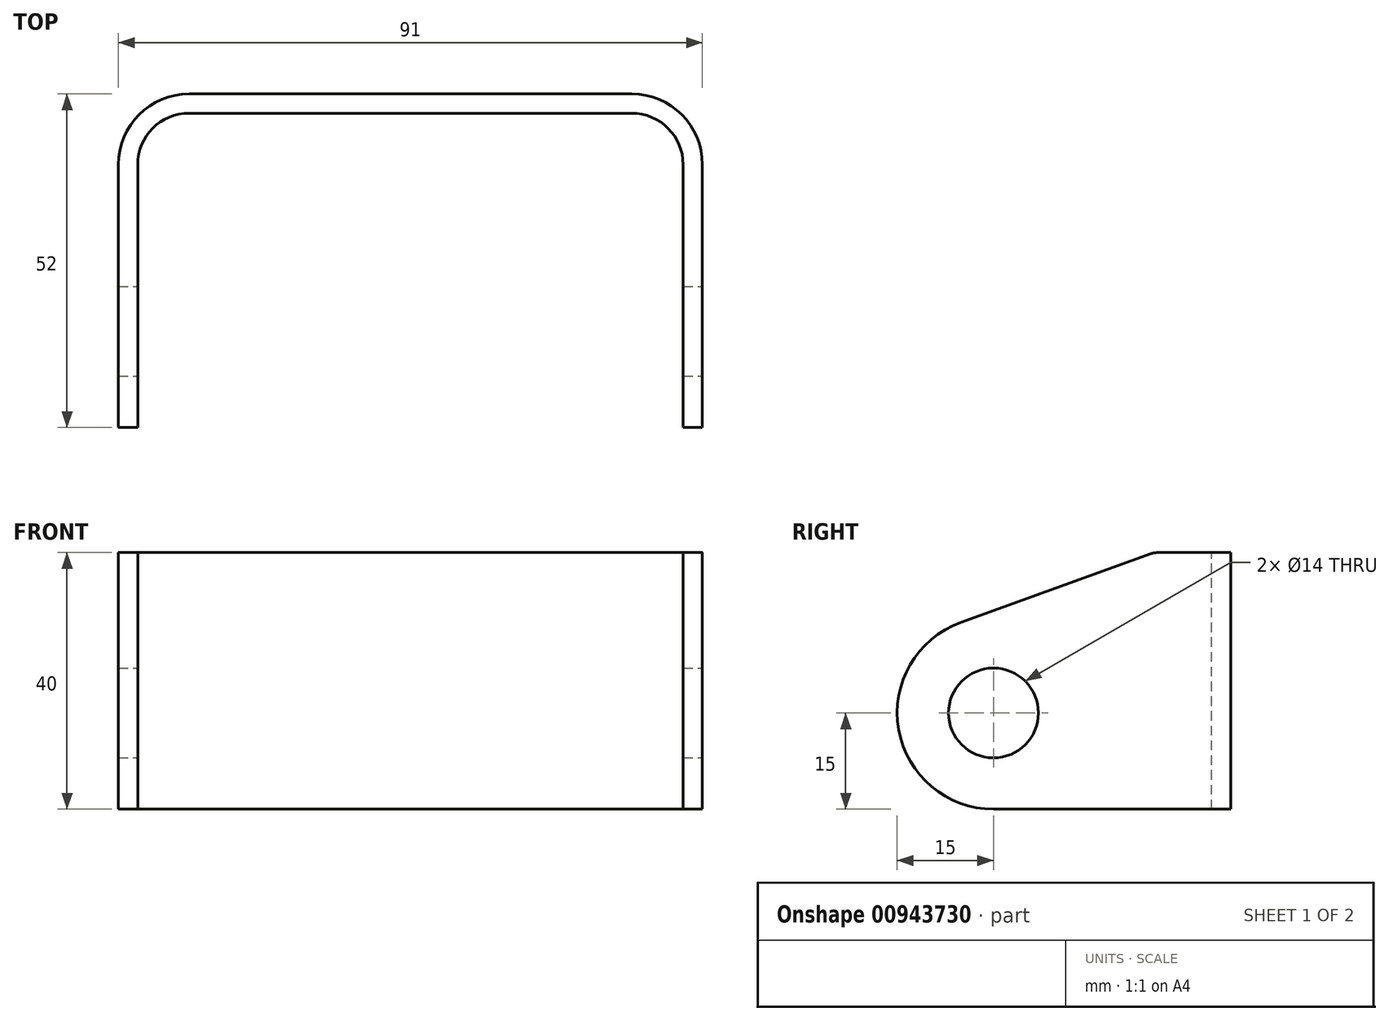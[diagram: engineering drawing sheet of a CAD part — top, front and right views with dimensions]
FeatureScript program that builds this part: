
annotation { "Feature Type Name" : "Feature", "Feature Type Description" : "" }
export const myFeature = defineFeature(function(context is Context, id is Id, definition is map)
    precondition{}
    {
        {
            var Q0;
            Q0=qCreatedBy(makeId("Right.planeOp"),FACE);
            var sketch = newSketch(context, id + "F0", { "sketchPlane" : qUnion([Q0])});
            skCircle(sketch, "E0", {"center": v(0, 0) * mm, "radius": 15 * mm});
            skLineSegment(sketch, "E1", {"start": v(0, -15) * mm, "end": v(37, -15) * mm});
            skLineSegment(sketch, "E2", {"start": v(37, -15) * mm, "end": v(37, 25) * mm});
            skLineSegment(sketch, "E3", {"start": v(37, 25) * mm, "end": v(25, 25) * mm});
            skLineSegment(sketch, "E4", {"start": v(25, 25) * mm, "end": v(-5.1, 14.1) * mm});
            skCircle(sketch, "E5", {"center": v(0, 0) * mm, "radius": 7 * mm});
            skSolve(sketch);
        }
        {
            var Q0;
            {var subQ0=sQuery(id+"F0.wireOp",EDGE,"E1");Q0=makeQuery(id+"F0.imprint","IMPRINT",FACE,{"disambiguationData":[TD([[makeQuery(id+"F0.imprint","IMPRINT",EDGE,{"derivedFrom":subQ0}),1.0]])]});}
            var Q1;
            Q1=makeQuery(id+"F0.imprint","IMPRINT",FACE,{"disambiguationData":[TD([[makeQuery(id+"F0.imprint","IMPRINT",EDGE,{"derivedFrom":sQuery(id+"F0.wireOp",EDGE,"E5")}),-1.0]])]});
            var Q2;
            Q2=makeQuery(id+"F0.imprint","IMPRINT",FACE,{"disambiguationData":[TD([[makeQuery(id+"F0.imprint","IMPRINT",EDGE,{"derivedFrom":sQuery(id+"F0.wireOp",EDGE,"E5")}),1.0]])]});
            extrude(context, id + "F1", {"entities" : qUnion([Q0, Q1, Q2]), "oppositeDirection" : true, "depth" : 91 * mm, "offsetDistance" : 25 * mm});
        }
        {
            var Q0;
            Q0=makeQuery(id+"F1.opExtrude","CAP_EDGE",EDGE,{"disambiguationData":[OSD([sQuery(id+"F0.wireOp",EDGE,"E2")])],"isStart":true});
            var Q1;
            Q1=makeQuery(id+"F1.opExtrude","CAP_EDGE",EDGE,{"disambiguationData":[OSD([sQuery(id+"F0.wireOp",EDGE,"E2")])],"isStart":false});
            fillet(context, id + "F2", {"entities" : qUnion([Q0, Q1]), "radius" : 11 * mm, "tangentPropagation" : true, "allowEdgeOverflow" : false});
        }
        {
            var Q0;
            Q0=makeQuery(id+"F1.opExtrude","SWEPT_FACE",FACE,{"disambiguationData":[OSD([sQuery(id+"F0.wireOp",EDGE,"E0")])]});
            var Q1;
            Q1=makeQuery(id+"F1.opExtrude","SWEPT_FACE",FACE,{"disambiguationData":[OSD([sQuery(id+"F0.wireOp",EDGE,"E1")])]});
            var Q2;
            Q2=makeQuery(id+"F1.opExtrude","SWEPT_FACE",FACE,{"disambiguationData":[OSD([sQuery(id+"F0.wireOp",EDGE,"E4")])]});
            var Q3;
            Q3=makeQuery(id+"F1.opExtrude","SWEPT_FACE",FACE,{"disambiguationData":[OSD([sQuery(id+"F0.wireOp",EDGE,"E3")])]});
            shell(context, id + "F3", {"entities" : qUnion([Q0, Q1, Q2, Q3]), "thickness" : 3 * mm});
        }
        {
            var Q0;
            Q0=makeQuery(id+"F0.imprint","IMPRINT",FACE,{"disambiguationData":[TD([[makeQuery(id+"F0.imprint","IMPRINT",EDGE,{"derivedFrom":sQuery(id+"F0.wireOp",EDGE,"E5")}),1.0]])]});
            extrude(context, id + "F4", {"entities" : qUnion([Q0]), "operationType" : NewBodyOperationType.REMOVE, "oppositeDirection" : true, "depth" : 100 * mm, "offsetDistance" : 25 * mm});
        }
        {
            var Q0;
            Q0=makeQuery(id+"F3.opShell","OFFSET_EDGE",EDGE,{"disambiguationData":[OSD([sQuery(id+"F0.wireOp",EDGE,"E3"),sQuery(id+"F0.wireOp",EDGE,"E4")])]});
            var Q1;
            Q1=makeQuery(id+"F1.opExtrude","SWEPT_EDGE",EDGE,{"disambiguationData":[OSD([sQuery(id+"F0.wireOp",EDGE,"E3"),sQuery(id+"F0.wireOp",EDGE,"E4")])]});
            fillet(context, id + "F5", {"entities" : qUnion([Q0, Q1]), "radius" : 3 * mm, "tangentPropagation" : true, "allowEdgeOverflow" : false});
        }
    });
